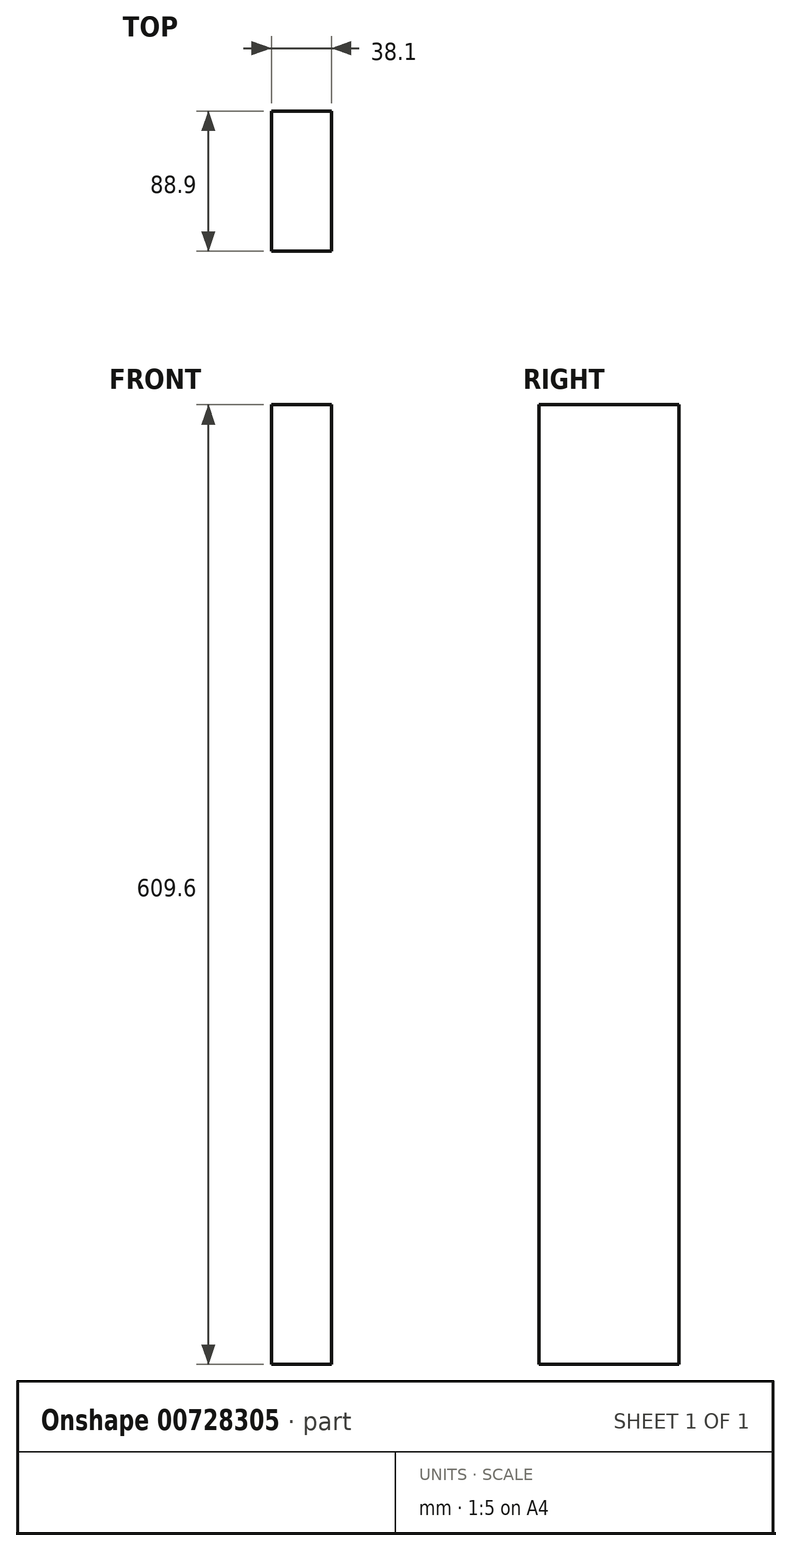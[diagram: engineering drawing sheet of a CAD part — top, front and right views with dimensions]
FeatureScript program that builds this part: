
annotation { "Feature Type Name" : "Feature", "Feature Type Description" : "" }
export const myFeature = defineFeature(function(context is Context, id is Id, definition is map)
    precondition{}
    {
        {
            var Q0;
            Q0=qCreatedBy(makeId("Front.planeOp"),FACE);
            var sketch = newSketch(context, id + "F0", { "sketchPlane" : qUnion([Q0])});
            skLineSegment(sketch, "E0.bottom", {"start": v(-19.05, -304.8) * mm, "end": v(19.05, -304.8) * mm});
            skLineSegment(sketch, "E0.top", {"start": v(-19.05, 304.8) * mm, "end": v(19.05, 304.8) * mm});
            skLineSegment(sketch, "E0.left", {"start": v(-19.05, -304.8) * mm, "end": v(-19.05, 304.8) * mm});
            skLineSegment(sketch, "E0.right", {"start": v(19.05, -304.8) * mm, "end": v(19.05, 304.8) * mm});
            skPoint(sketch, "E0.middle", {"position": v(0, 0) * mm});
            skSolve(sketch);
        }
        {
            var Q0;
            Q0=qSketchRegion(id+"F0",true);
            extrude(context, id + "F1", {"entities" : qUnion([Q0]), "depth" : 88.9 * mm, "offsetDistance" : 25.4 * mm});
        }
    });
